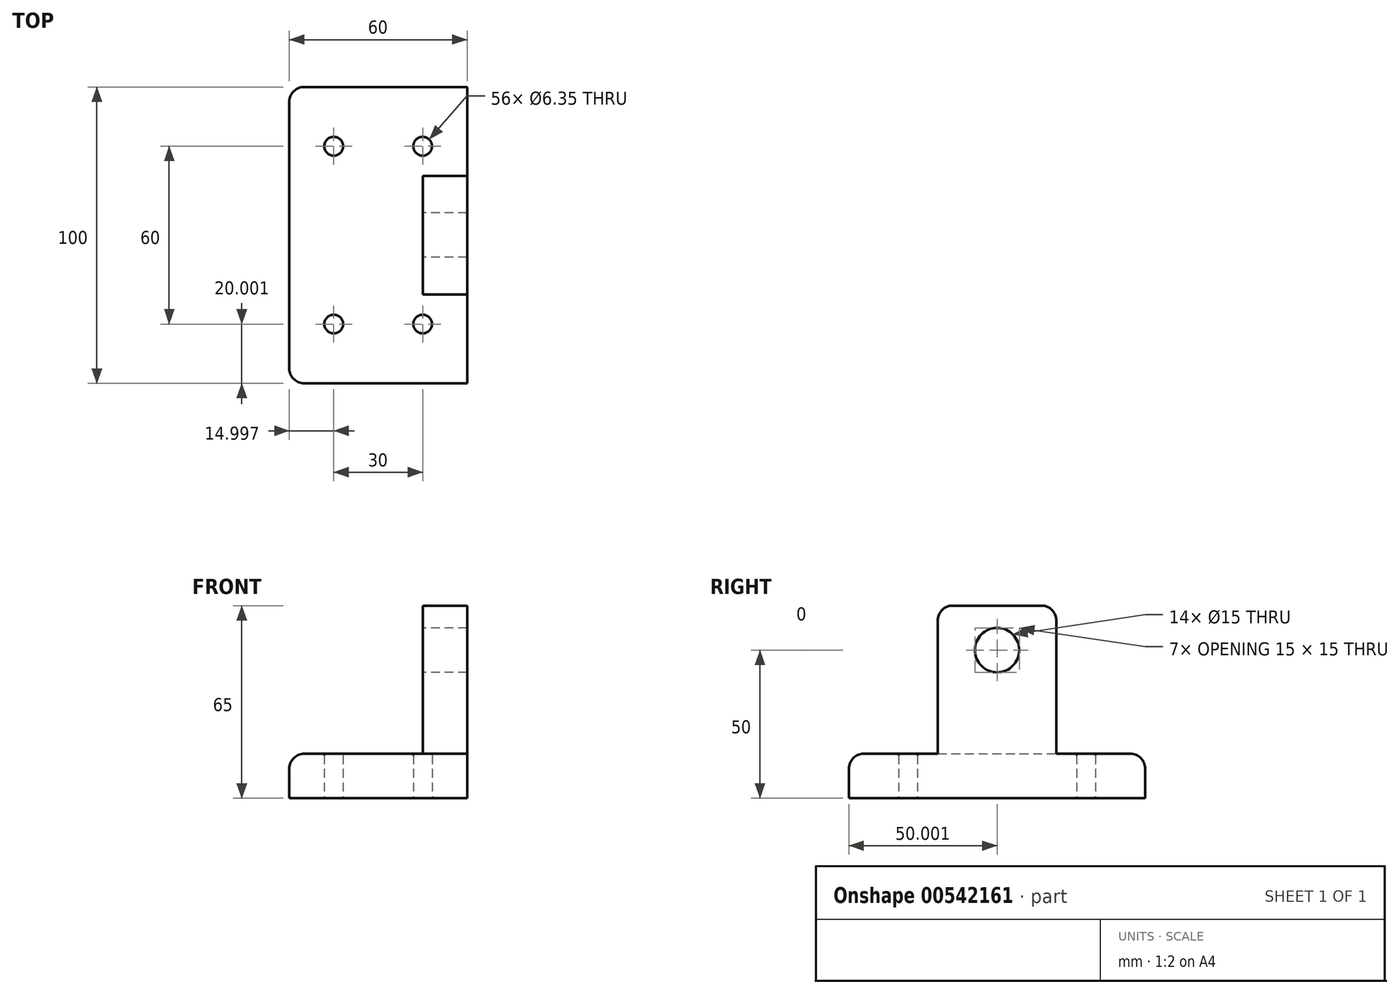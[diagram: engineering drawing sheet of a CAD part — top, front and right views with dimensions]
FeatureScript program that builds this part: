
annotation { "Feature Type Name" : "Feature", "Feature Type Description" : "" }
export const myFeature = defineFeature(function(context is Context, id is Id, definition is map)
    precondition{}
    {
        {
            var Q0;
            Q0=qCreatedBy(makeId("Top.planeOp"),FACE);
            var sketch = newSketch(context, id + "F0", { "sketchPlane" : qUnion([Q0])});
            skLineSegment(sketch, "E0.bottom", {"start": v(-33.56, -33.35) * mm, "end": v(21.44, -33.35) * mm});
            skLineSegment(sketch, "E0.top", {"start": v(-33.56, 66.65) * mm, "end": v(21.44, 66.65) * mm});
            skLineSegment(sketch, "E0.left", {"start": v(-38.56, -28.35) * mm, "end": v(-38.56, 61.65) * mm});
            skLineSegment(sketch, "E0.right", {"start": v(21.44, -33.35) * mm, "end": v(21.44, 66.65) * mm});
            skPoint(sketch, "E1.visualSharp", {"position": v(-38.56, 66.65) * mm});
            skArc(sketch, "E1.filletArc", {"start": v(-33.56, 66.65) * mm, "mid": v(-37.1, 65.19) * mm, "end": v(-38.56, 61.65) * mm});
            skPoint(sketch, "E2.visualSharp", {"position": v(-38.56, -33.35) * mm});
            skArc(sketch, "E2.filletArc", {"start": v(-38.56, -28.35) * mm, "mid": v(-37.1, -31.89) * mm, "end": v(-33.56, -33.35) * mm});
            skSolve(sketch);
        }
        {
            var Q0;
            Q0 = qSketchRegion(id + "F0", true);
            extrude(context, id + "F1", {"entities" : qUnion([Q0]), "depth" : 15 * mm, "offsetDistance" : 25 * mm});
        }
        {
            var Q0;
            Q0=makeQuery(id+"F1.opExtrude","SWEPT_FACE",FACE,{"disambiguationData":[OSD([sQuery(id+"F0.wireOp",EDGE,"E0.right")])]});
            var sketch = newSketch(context, id + "F2", { "sketchPlane" : qUnion([Q0])});
            skLineSegment(sketch, "E3.bottom", {"start": v(-3.35, 15) * mm, "end": v(36.65, 15) * mm});
            skLineSegment(sketch, "E3.top", {"start": v(-3.35, 65) * mm, "end": v(36.65, 65) * mm});
            skLineSegment(sketch, "E3.left", {"start": v(-3.35, 15) * mm, "end": v(-3.35, 65) * mm});
            skLineSegment(sketch, "E3.right", {"start": v(36.65, 15) * mm, "end": v(36.65, 65) * mm});
            skSolve(sketch);
        }
        {
            var Q0;
            Q0 = qSketchRegion(id + "F2", true);
            extrude(context, id + "F3", {"entities" : qUnion([Q0]), "oppositeDirection" : true, "depth" : 15 * mm, "offsetDistance" : 25 * mm});
        }
        {
            var Q0;
            Q0=makeQuery(id+"F3.opExtrude","SWEPT_BODY",BODY,{"disambiguationData":[OSD([sQuery(id+"F2.wireOp",EDGE,"E3.bottom"),sQuery(id+"F2.wireOp",EDGE,"E3.top"),sQuery(id+"F2.wireOp",EDGE,"E3.left"),sQuery(id+"F2.wireOp",EDGE,"E3.right")])]});
            var Q1;
            Q1=makeQuery(id+"F1.opExtrude","SWEPT_BODY",BODY,{"disambiguationData":[OSD([sQuery(id+"F0.wireOp",EDGE,"E0.bottom"),sQuery(id+"F0.wireOp",EDGE,"E0.top"),sQuery(id+"F0.wireOp",EDGE,"E0.left"),sQuery(id+"F0.wireOp",EDGE,"E0.right"),sQuery(id+"F0.wireOp",EDGE,"E1.filletArc"),sQuery(id+"F0.wireOp",EDGE,"E2.filletArc")])]});
            booleanBodies(context, id + "F4", {"operationType" : BooleanOperationType.UNION, "tools" : qUnion([Q0, Q1])});
        }
        {
            var Q0;
            Q0=makeQuery(id+"F3.opExtrude","CAP_EDGE",EDGE,{"disambiguationData":[OSD([sQuery(id+"F2.wireOp",EDGE,"E3.bottom")])],"isStart":false});
            var Q1;
            Q1=makeQuery(id+"F3.opExtrude","SWEPT_EDGE",EDGE,{"disambiguationData":[OSD([sQuery(id+"F0.wireOp",EDGE,"E0.right"),sQuery(id+"F2.wireOp",EDGE,"E3.bottom"),sQuery(id+"F2.wireOp",EDGE,"E3.left")])]});
            var Q2;
            Q2=makeQuery(id+"F3.opExtrude","SWEPT_EDGE",EDGE,{"disambiguationData":[OSD([sQuery(id+"F2.wireOp",EDGE,"E3.top"),sQuery(id+"F2.wireOp",EDGE,"E3.left")])]});
            var Q3;
            Q3=makeQuery(id+"F3.opExtrude","SWEPT_EDGE",EDGE,{"disambiguationData":[OSD([sQuery(id+"F2.wireOp",EDGE,"E3.top"),sQuery(id+"F2.wireOp",EDGE,"E3.right")])]});
            var Q4;
            Q4=makeQuery(id+"F3.opExtrude","SWEPT_EDGE",EDGE,{"disambiguationData":[OSD([sQuery(id+"F0.wireOp",EDGE,"E0.right"),sQuery(id+"F2.wireOp",EDGE,"E3.bottom"),sQuery(id+"F2.wireOp",EDGE,"E3.right")])]});
            var Q5;
            Q5=makeQuery(id+"F1.opExtrude","CAP_EDGE",EDGE,{"disambiguationData":[OSD([sQuery(id+"F0.wireOp",EDGE,"E0.top")])],"isStart":false});
            fillet(context, id + "F5", {"entities" : qUnion([Q0, Q1, Q2, Q3, Q4, Q5]), "radius" : 5 * mm, "tangentPropagation" : true, "allowEdgeOverflow" : false});
        }
        {
            var Q0;
            Q0=makeQuery(id+"F3.opExtrude","CAP_FACE",FACE,{"disambiguationData":[OSD([sQuery(id+"F2.wireOp",EDGE,"E3.bottom"),sQuery(id+"F2.wireOp",EDGE,"E3.top"),sQuery(id+"F2.wireOp",EDGE,"E3.left"),sQuery(id+"F2.wireOp",EDGE,"E3.right")])],"isStart":false});
            var sketch = newSketch(context, id + "F6", { "sketchPlane" : qUnion([Q0])});
            skPoint(sketch, "E4", {"position": v(-16.65, 65) * mm});
            skCircle(sketch, "E5", {"center": v(-16.65, 50) * mm, "radius": 7.5 * mm});
            skSolve(sketch);
        }
        {
            var Q0;
            Q0 = qSketchRegion(id + "F6", true);
            extrude(context, id + "F7", {"entities" : qUnion([Q0]), "operationType" : NewBodyOperationType.REMOVE, "oppositeDirection" : true, "depth" : 25 * mm, "offsetDistance" : 25 * mm});
        }
        {
            var Q0;
            Q0=makeQuery(id+"F1.opExtrude","CAP_FACE",FACE,{"disambiguationData":[OSD([sQuery(id+"F0.wireOp",EDGE,"E0.bottom"),sQuery(id+"F0.wireOp",EDGE,"E0.top"),sQuery(id+"F0.wireOp",EDGE,"E0.left"),sQuery(id+"F0.wireOp",EDGE,"E0.right"),sQuery(id+"F0.wireOp",EDGE,"E1.filletArc"),sQuery(id+"F0.wireOp",EDGE,"E2.filletArc")])],"isStart":true});
            var sketch = newSketch(context, id + "F8", { "sketchPlane" : qUnion([Q0])});
            skCircle(sketch, "E6", {"center": v(-23.56, -46.65) * mm, "radius": 3.17 * mm});
            skCircle(sketch, "E7.0.1.0", {"center": v(-23.56, 13.35) * mm, "radius": 3.17 * mm});
            skCircle(sketch, "E7.1.0.0", {"center": v(6.44, -46.65) * mm, "radius": 3.17 * mm});
            skCircle(sketch, "E7.1.1.0", {"center": v(6.44, 13.35) * mm, "radius": 3.17 * mm});
            skLineSegment(sketch, "E7.direction1", {"start": v(-23.56, -46.65) * mm, "end": v(6.44, -46.65) * mm, "construction": true});
            skLineSegment(sketch, "E7.direction2", {"start": v(-23.56, -46.65) * mm, "end": v(-23.56, 13.35) * mm, "construction": true});
            skSolve(sketch);
        }
        {
            var Q0;
            Q0=makeQuery(id+"F8.imprint","IMPRINT",FACE,{"disambiguationData":[TD([[makeQuery(id+"F8.imprint","IMPRINT",EDGE,{"derivedFrom":sQuery(id+"F8.wireOp",EDGE,"E6")}),1.0]])]});
            var Q1;
            Q1=makeQuery(id+"F8.imprint","IMPRINT",FACE,{"disambiguationData":[TD([[makeQuery(id+"F8.imprint","IMPRINT",EDGE,{"derivedFrom":sQuery(id+"F8.wireOp",EDGE,"E7.1.0.0")}),1.0]])]});
            var Q2;
            Q2=makeQuery(id+"F8.imprint","IMPRINT",FACE,{"disambiguationData":[TD([[makeQuery(id+"F8.imprint","IMPRINT",EDGE,{"derivedFrom":sQuery(id+"F8.wireOp",EDGE,"E7.1.1.0")}),1.0]])]});
            var Q3;
            Q3=makeQuery(id+"F8.imprint","IMPRINT",FACE,{"disambiguationData":[TD([[makeQuery(id+"F8.imprint","IMPRINT",EDGE,{"derivedFrom":sQuery(id+"F8.wireOp",EDGE,"E7.0.1.0")}),1.0]])]});
            extrude(context, id + "F9", {"entities" : qUnion([Q0, Q1, Q2, Q3]), "operationType" : NewBodyOperationType.REMOVE, "oppositeDirection" : true, "depth" : 25 * mm, "offsetDistance" : 25 * mm});
        }
        {
            var Q0;
            Q0=makeQuery(id+"F9.boolean.opBoolean","INTERSECT",EDGE,{"derivedFrom":[makeQuery(id+"F1.opExtrude","CAP_FACE",FACE,{"disambiguationData":[OSD([sQuery(id+"F0.wireOp",EDGE,"E0.bottom"),sQuery(id+"F0.wireOp",EDGE,"E0.top"),sQuery(id+"F0.wireOp",EDGE,"E0.left"),sQuery(id+"F0.wireOp",EDGE,"E0.right"),sQuery(id+"F0.wireOp",EDGE,"E1.filletArc"),sQuery(id+"F0.wireOp",EDGE,"E2.filletArc")])],"isStart":false}),makeQuery(id+"F9.opExtrude","SWEPT_FACE",FACE,{"disambiguationData":[OSD([sQuery(id+"F8.wireOp",EDGE,"E7.1.1.0")])]})]});
            var Q1;
            Q1=makeQuery(id+"F9.boolean.opBoolean","INTERSECT",EDGE,{"derivedFrom":[makeQuery(id+"F1.opExtrude","CAP_FACE",FACE,{"disambiguationData":[OSD([sQuery(id+"F0.wireOp",EDGE,"E0.bottom"),sQuery(id+"F0.wireOp",EDGE,"E0.top"),sQuery(id+"F0.wireOp",EDGE,"E0.left"),sQuery(id+"F0.wireOp",EDGE,"E0.right"),sQuery(id+"F0.wireOp",EDGE,"E1.filletArc"),sQuery(id+"F0.wireOp",EDGE,"E2.filletArc")])],"isStart":false}),makeQuery(id+"F9.opExtrude","SWEPT_FACE",FACE,{"disambiguationData":[OSD([sQuery(id+"F8.wireOp",EDGE,"E7.0.1.0")])]})]});
            var Q2;
            Q2=makeQuery(id+"F9.boolean.opBoolean","INTERSECT",EDGE,{"derivedFrom":[makeQuery(id+"F1.opExtrude","CAP_FACE",FACE,{"disambiguationData":[OSD([sQuery(id+"F0.wireOp",EDGE,"E0.bottom"),sQuery(id+"F0.wireOp",EDGE,"E0.top"),sQuery(id+"F0.wireOp",EDGE,"E0.left"),sQuery(id+"F0.wireOp",EDGE,"E0.right"),sQuery(id+"F0.wireOp",EDGE,"E1.filletArc"),sQuery(id+"F0.wireOp",EDGE,"E2.filletArc")])],"isStart":false}),makeQuery(id+"F9.opExtrude","SWEPT_FACE",FACE,{"disambiguationData":[OSD([sQuery(id+"F8.wireOp",EDGE,"E6")])]})]});
            var Q3;
            Q3=makeQuery(id+"F9.boolean.opBoolean","INTERSECT",EDGE,{"derivedFrom":[makeQuery(id+"F1.opExtrude","CAP_FACE",FACE,{"disambiguationData":[OSD([sQuery(id+"F0.wireOp",EDGE,"E0.bottom"),sQuery(id+"F0.wireOp",EDGE,"E0.top"),sQuery(id+"F0.wireOp",EDGE,"E0.left"),sQuery(id+"F0.wireOp",EDGE,"E0.right"),sQuery(id+"F0.wireOp",EDGE,"E1.filletArc"),sQuery(id+"F0.wireOp",EDGE,"E2.filletArc")])],"isStart":false}),makeQuery(id+"F9.opExtrude","SWEPT_FACE",FACE,{"disambiguationData":[OSD([sQuery(id+"F8.wireOp",EDGE,"E7.1.0.0")])]})]});
            fillet(context, id + "F10", {"entities" : qUnion([Q0, Q1, Q2, Q3]), "radius" : 0.5 * mm, "tangentPropagation" : true, "allowEdgeOverflow" : false});
        }
    });
